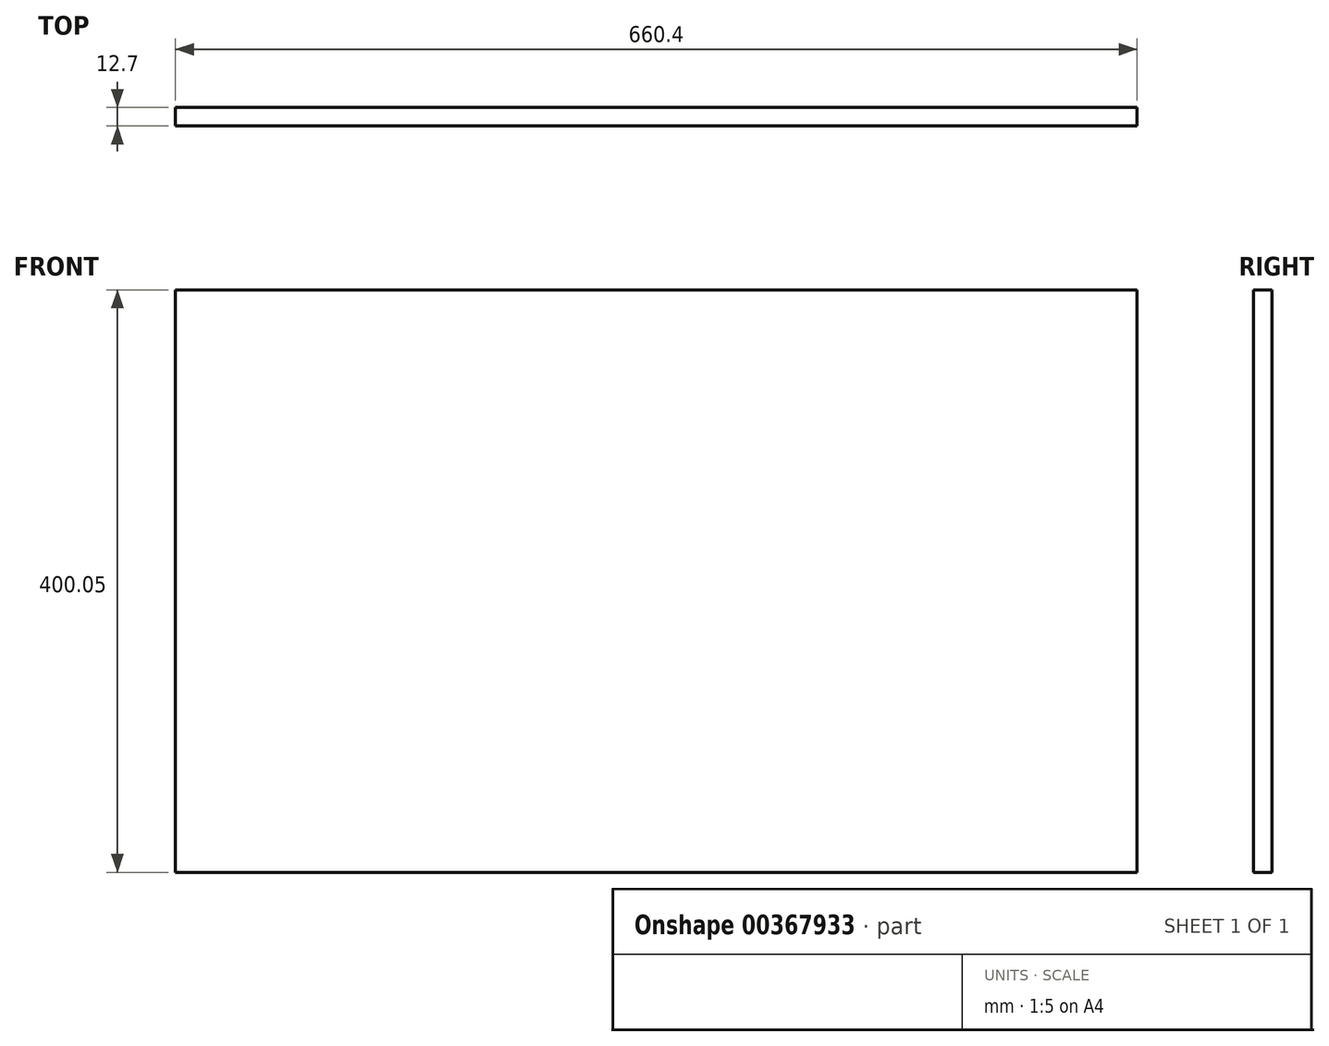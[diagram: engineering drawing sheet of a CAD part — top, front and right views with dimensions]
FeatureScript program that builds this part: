
annotation { "Feature Type Name" : "Feature", "Feature Type Description" : "" }
export const myFeature = defineFeature(function(context is Context, id is Id, definition is map)
    precondition{}
    {
        {
            var Q0;
            Q0=qCreatedBy(makeId("Front.planeOp"),FACE);
            var sketch = newSketch(context, id + "F0", { "sketchPlane" : qUnion([Q0])});
            skLineSegment(sketch, "E0.bottom", {"start": v(-332.95, 49.29) * mm, "end": v(327.45, 49.29) * mm});
            skLineSegment(sketch, "E0.top", {"start": v(-332.95, -350.76) * mm, "end": v(327.45, -350.76) * mm});
            skLineSegment(sketch, "E0.left", {"start": v(-332.95, 49.29) * mm, "end": v(-332.95, -350.76) * mm});
            skLineSegment(sketch, "E0.right", {"start": v(327.45, 49.29) * mm, "end": v(327.45, -350.76) * mm});
            skSolve(sketch);
        }
        {
            var Q0;
            Q0=makeQuery(id+"F0.imprint","IMPRINT",FACE,{"disambiguationData":[TD([[makeQuery(id+"F0.imprint","IMPRINT",EDGE,{"derivedFrom":sQuery(id+"F0.wireOp",EDGE,"E0.bottom")}),-1.0]])]});
            extrude(context, id + "F1", {"entities" : qUnion([Q0]), "depth" : 12.7 * mm});
        }
    });
